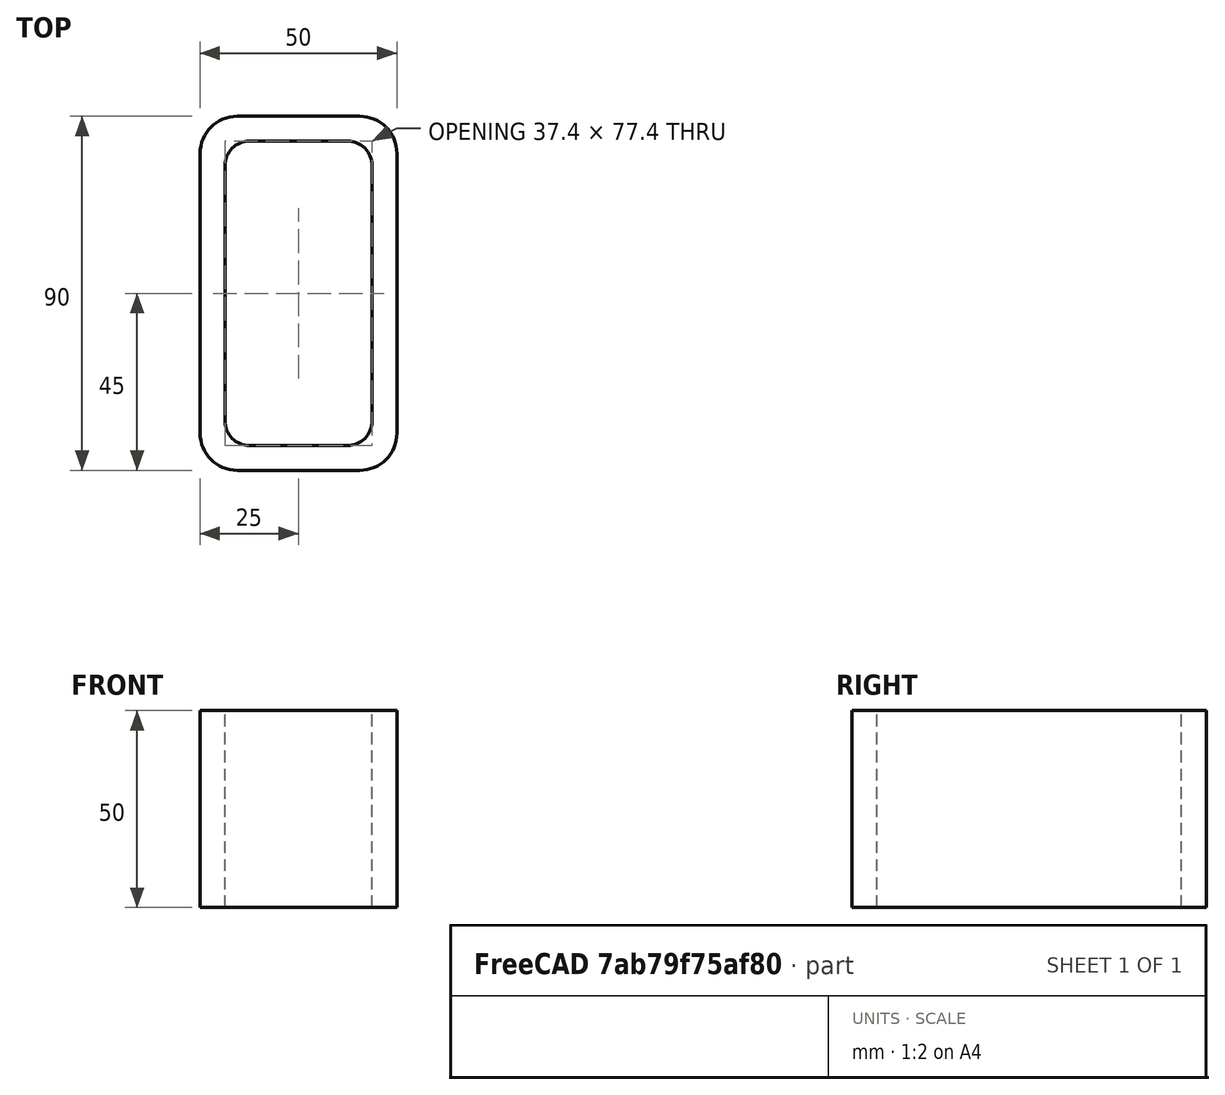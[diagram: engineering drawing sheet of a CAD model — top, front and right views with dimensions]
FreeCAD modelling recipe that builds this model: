
FCSTD DOCUMENT  (FreeCAD 0.15R4671 (Git))
Label: Rectangular hollow section 90x50x6.3 EN10219 S235JRH
License: All rights reserved
LicenseURL: http://en.wikipedia.org/wiki/All_rights_reserved
objects: Sketcher::SketchObject×1, Part::Extrusion×1
note: 2 computed .brp shape members not serialized (recipe doc carries the construction recipe); baked Part::Feature solids carry a one-line shape summary decoded from their .brp

FEATURE [Sketcher::SketchObject] Sketch
  sketch-geometry (16):
    g0: LineSegment StartX=-12.4 StartY=38.7 StartZ=0 EndX=12.4 EndY=38.7 EndZ=0
    g1: LineSegment StartX=18.7 StartY=32.4 StartZ=0 EndX=18.7 EndY=-32.4 EndZ=0
    g2: LineSegment StartX=12.4 StartY=-38.7 StartZ=0 EndX=-12.4 EndY=-38.7 EndZ=0
    g3: LineSegment StartX=-18.7 StartY=-32.4 StartZ=0 EndX=-18.7 EndY=32.4 EndZ=0
    g4: LineSegment StartX=-15.55 StartY=45 StartZ=0 EndX=15.55 EndY=45 EndZ=0
    g5: LineSegment StartX=25 StartY=35.55 StartZ=0 EndX=25 EndY=-35.55 EndZ=0
    g6: LineSegment StartX=15.55 StartY=-45 StartZ=0 EndX=-15.55 EndY=-45 EndZ=0
    g7: LineSegment StartX=-25 StartY=-35.55 StartZ=0 EndX=-25 EndY=35.55 EndZ=0
    g8: ArcOfCircle CenterX=-12.4 CenterY=32.4 CenterZ=0 NormalX=0 NormalY=0 NormalZ=1 Radius=6.3 StartAngle=1.5708 EndAngle=3.14159
    g9: ArcOfCircle CenterX=12.4 CenterY=32.4 CenterZ=0 NormalX=0 NormalY=0 NormalZ=1 Radius=6.3 StartAngle=0 EndAngle=1.5708
    g10: ArcOfCircle CenterX=12.4 CenterY=-32.4 CenterZ=0 NormalX=0 NormalY=0 NormalZ=1 Radius=6.3 StartAngle=4.71239 EndAngle=6.28319
    g11: ArcOfCircle CenterX=-12.4 CenterY=-32.4 CenterZ=0 NormalX=0 NormalY=0 NormalZ=1 Radius=6.3 StartAngle=3.14159 EndAngle=4.71239
    g12: ArcOfCircle CenterX=15.55 CenterY=35.55 CenterZ=0 NormalX=0 NormalY=0 NormalZ=1 Radius=9.45 StartAngle=0 EndAngle=1.5708
    g13: ArcOfCircle CenterX=15.55 CenterY=-35.55 CenterZ=0 NormalX=0 NormalY=0 NormalZ=1 Radius=9.45 StartAngle=4.71239 EndAngle=6.28319
    g14: ArcOfCircle CenterX=-15.55 CenterY=-35.55 CenterZ=0 NormalX=0 NormalY=0 NormalZ=1 Radius=9.45 StartAngle=3.14159 EndAngle=4.71239
    g15: ArcOfCircle CenterX=-15.55 CenterY=35.55 CenterZ=0 NormalX=0 NormalY=0 NormalZ=1 Radius=9.45 StartAngle=1.5708 EndAngle=3.14159
  constraints (36):
    c: Horizontal(g2)
    c: Vertical(g3)
    c: Horizontal(g6)
    c: Vertical(g7)
    c: Tangent(g3,g8) = 1.5708
    c: Tangent(g0,g8) = 1.5708
    c: Tangent(g0,g9) = 1.5708
    c: Tangent(g1,g9) = 1.5708
    c: Tangent(g1,g10) = 1.5708
    c: Tangent(g2,g10) = 1.5708
    c: Tangent(g2,g11) = 1.5708
    c: Tangent(g3,g11) = 1.5708
    c: Tangent(g4,g12) = 1.5708
    c: Tangent(g5,g12) = 1.5708
    c: Tangent(g5,g13) = 1.5708
    c: Tangent(g6,g13) = 1.5708
    c: Tangent(g6,g14) = 1.5708
    c: Tangent(g7,g14) = 1.5708
    c: Tangent(g7,g15) = 1.5708
    c: Tangent(g4,g15) = 1.5708
    c: Equal(g9,g8)
    c: Equal(g9,g11)
    c: Equal(g9,g10)
    c: Equal(g12,g15)
    c: Equal(g12,g14)
    c: Equal(g12,g13)
    c: Symmetric(g4,g6,g-1)
    c: Symmetric(g7,g5,g-2)
    c: DistanceY(g4,g6) = -90
    c: DistanceX(g7,g5) = 50
    c: Symmetric(g3,g1,g-2)
    c: Symmetric(g0,g2,g-1)
    c: DistanceY(g0,g4) = 6.3
    c: DistanceX(g5,g1) = -6.3
    c: Radius(g9) = 6.3
    c: Radius(g12) = 9.45
FEATURE [Part::Extrusion] Extrude  label="Rectangular hollow section 90x50x6.3 EN10219 S235JRH"
  Base = -> Sketch
  Dir = (0,0,50)
  Solid = true
